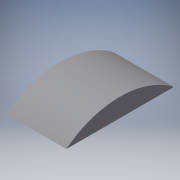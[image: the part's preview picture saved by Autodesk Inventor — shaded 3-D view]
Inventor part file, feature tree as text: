
AUTODESK INVENTOR PART (.ipt)
format: ipt  version: 2018 (Build 220112000, 112)  size: 92,160 bytes
history: native  units: in
note: dims shown in document units (in); Inventor stores cm internally (conversion verified against a paired STEP export)
features: extrude x1, sketch x1
ambient origin geometry x8: Origin, YZ Plane, XZ Plane, XY Plane, X Axis, Y Axis, Z Axis, Center Point
bodies: Solid1 (feature_tree)
feature tree (2):
  extrude  "Extrusion1"  TaperAngle=90.0deg  [1 undecoded]
  sketch  "Sketch1"  dims[d0=46.5in d1=90.0deg d3=26.0in d4=0.0in]
note: 1 required parameter value undecoded (feature->parameter linkage not recoverable at this tier; creation-order binding heuristic only, values carry confidence <= 0.55)
